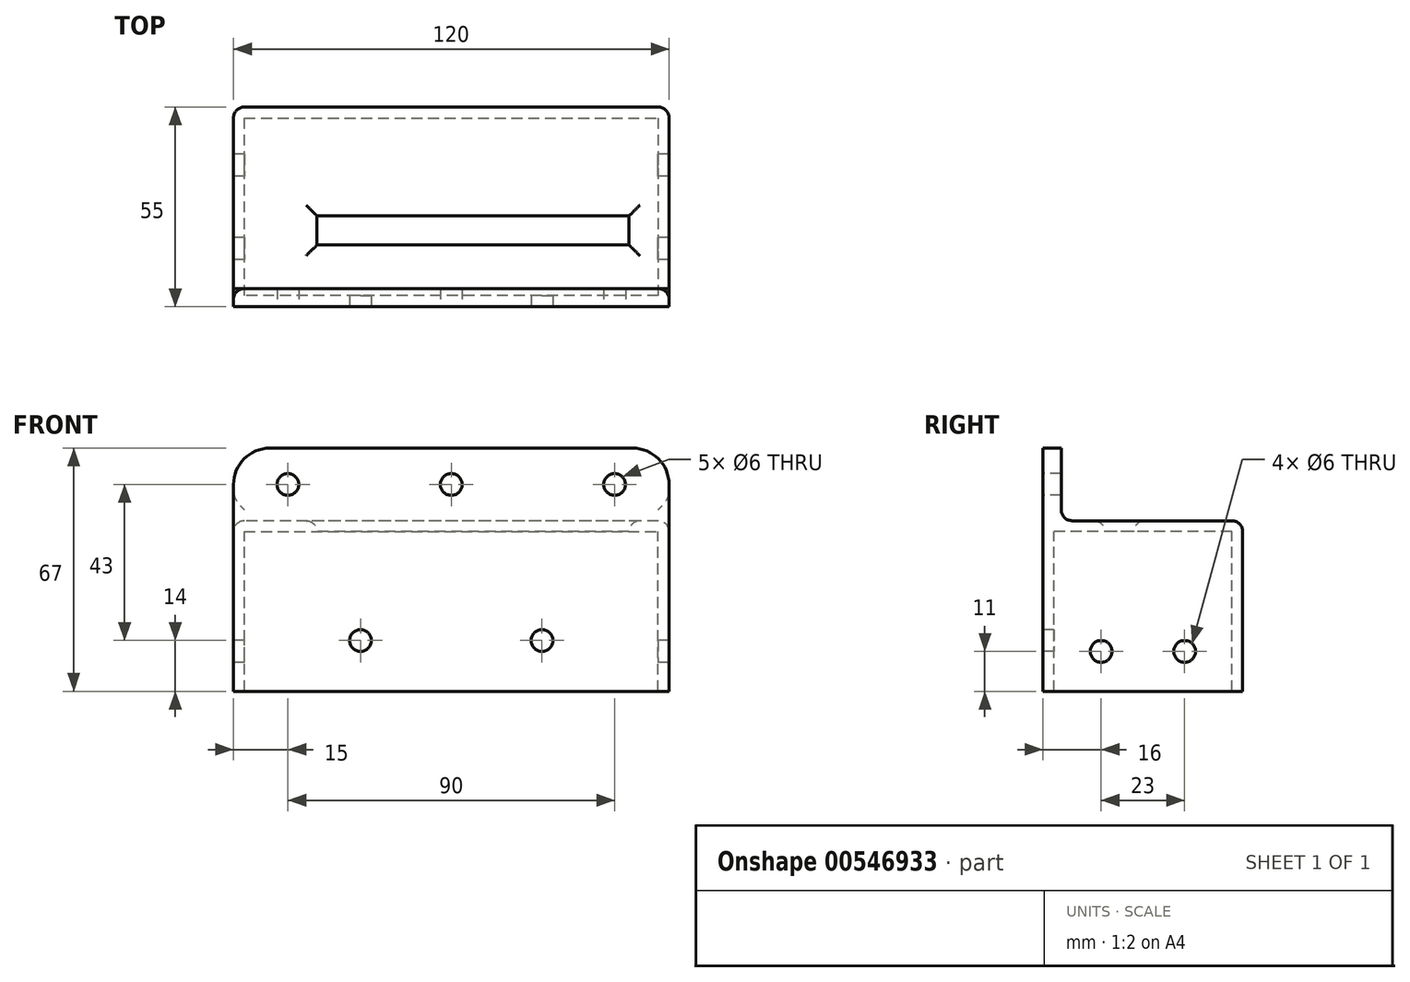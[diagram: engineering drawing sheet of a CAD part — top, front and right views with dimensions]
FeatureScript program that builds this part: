
annotation { "Feature Type Name" : "Feature", "Feature Type Description" : "" }
export const myFeature = defineFeature(function(context is Context, id is Id, definition is map)
    precondition{}
    {
        {
            var Q0;
            Q0=qCreatedBy(makeId("Top.planeOp"),FACE);
            var sketch = newSketch(context, id + "F0", { "sketchPlane" : qUnion([Q0])});
            skLineSegment(sketch, "E0", {"start": v(0, 0) * mm, "end": v(0, 55) * mm});
            skLineSegment(sketch, "E1", {"start": v(0, 55) * mm, "end": v(120, 55) * mm});
            skLineSegment(sketch, "E2", {"start": v(120, 55) * mm, "end": v(120, 0) * mm});
            skLineSegment(sketch, "E3", {"start": v(120, 0) * mm, "end": v(0, 0) * mm});
            skLineSegment(sketch, "E4.0", {"start": v(3, 3) * mm, "end": v(3, 52) * mm});
            skLineSegment(sketch, "E5.0", {"start": v(117, 52) * mm, "end": v(117, 3) * mm});
            skLineSegment(sketch, "E6.0", {"start": v(3, 52) * mm, "end": v(117, 52) * mm});
            skLineSegment(sketch, "E7.0", {"start": v(117, 3) * mm, "end": v(3, 3) * mm});
            skLineSegment(sketch, "E8.0", {"start": v(109, 17) * mm, "end": v(23, 17) * mm});
            skLineSegment(sketch, "E9.0", {"start": v(109, 25) * mm, "end": v(23, 25) * mm});
            skLineSegment(sketch, "E10.0", {"start": v(23, 17) * mm, "end": v(23, 25) * mm});
            skLineSegment(sketch, "E11.0", {"start": v(109, 25) * mm, "end": v(109, 17) * mm});
            skSolve(sketch);
        }
        {
            var Q0;
            Q0=makeQuery(id+"F0.imprint","IMPRINT",FACE,{"disambiguationData":[TD([[makeQuery(id+"F0.imprint","IMPRINT",EDGE,{"derivedFrom":sQuery(id+"F0.wireOp",EDGE,"E4.0")}),-1.0]])]});
            extrude(context, id + "F1", {"entities" : qUnion([Q0]), "oppositeDirection" : true, "depth" : 3 * mm, "offsetDistance" : 25 * mm});
        }
        {
            var Q0;
            Q0=makeQuery(id+"F0.imprint","IMPRINT",FACE,{"disambiguationData":[TD([[makeQuery(id+"F0.imprint","IMPRINT",EDGE,{"derivedFrom":sQuery(id+"F0.wireOp",EDGE,"E0")}),-1.0]])]});
            extrude(context, id + "F2", {"entities" : qUnion([Q0]), "operationType" : NewBodyOperationType.ADD, "oppositeDirection" : true, "depth" : 47 * mm, "offsetDistance" : 25 * mm});
        }
        {
            var Q0;
            Q0=qCreatedBy(makeId("Right.planeOp"),FACE);
            var sketch = newSketch(context, id + "F3", { "sketchPlane" : qUnion([Q0])});
            skLineSegment(sketch, "E12", {"start": v(0, 0) * mm, "end": v(0, -36) * mm, "construction": true});
            skLineSegment(sketch, "E13", {"start": v(0, -36) * mm, "end": v(55, -36) * mm, "construction": true});
            skLineSegment(sketch, "E14.0", {"start": v(27.5, 0) * mm, "end": v(27.5, -36) * mm, "construction": true});
            skLineSegment(sketch, "E15.0", {"start": v(16, 0) * mm, "end": v(16, -36) * mm, "construction": true});
            skLineSegment(sketch, "E16.0", {"start": v(39, 0) * mm, "end": v(39, -36) * mm, "construction": true});
            skCircle(sketch, "E17", {"center": v(39, -36) * mm, "radius": 3 * mm});
            skCircle(sketch, "E18", {"center": v(16, -36) * mm, "radius": 3 * mm});
            skSolve(sketch);
        }
        {
            var Q0;
            Q0=makeQuery(id+"F3.imprint","IMPRINT",FACE,{"disambiguationData":[TD([[makeQuery(id+"F3.imprint","IMPRINT",EDGE,{"derivedFrom":sQuery(id+"F3.wireOp",EDGE,"E17")}),1.0]])]});
            var Q1;
            Q1=makeQuery(id+"F3.imprint","IMPRINT",FACE,{"disambiguationData":[TD([[makeQuery(id+"F3.imprint","IMPRINT",EDGE,{"derivedFrom":sQuery(id+"F3.wireOp",EDGE,"E18")}),1.0]])]});
            extrude(context, id + "F4", {"entities" : qUnion([Q0, Q1]), "operationType" : NewBodyOperationType.REMOVE, "depth" : 130 * mm, "offsetDistance" : 25 * mm});
        }
        {
            var Q0;
            Q0=qCreatedBy(makeId("Front.planeOp"),FACE);
            var sketch = newSketch(context, id + "F5", { "sketchPlane" : qUnion([Q0])});
            skLineSegment(sketch, "E19", {"start": v(0, 0) * mm, "end": v(120, 0) * mm, "construction": true});
            skLineSegment(sketch, "E20", {"start": v(0, 0) * mm, "end": v(0, -33) * mm, "construction": true});
            skLineSegment(sketch, "E21", {"start": v(0, -33) * mm, "end": v(122.32, -33) * mm, "construction": true});
            skLineSegment(sketch, "E22.0", {"start": v(60, 0) * mm, "end": v(60, -33) * mm, "construction": true});
            skLineSegment(sketch, "E23.0", {"start": v(35, 0) * mm, "end": v(35, -33) * mm, "construction": true});
            skLineSegment(sketch, "E24.0", {"start": v(85, 0) * mm, "end": v(85, -33) * mm, "construction": true});
            skCircle(sketch, "E25", {"center": v(35, -33) * mm, "radius": 3 * mm});
            skCircle(sketch, "E26", {"center": v(85, -33) * mm, "radius": 3 * mm});
            skSolve(sketch);
        }
        {
            var Q0;
            Q0=makeQuery(id+"F5.imprint","IMPRINT",FACE,{"disambiguationData":[TD([[makeQuery(id+"F5.imprint","IMPRINT",EDGE,{"derivedFrom":sQuery(id+"F5.wireOp",EDGE,"E25")}),1.0]])]});
            var Q1;
            Q1=makeQuery(id+"F5.imprint","IMPRINT",FACE,{"disambiguationData":[TD([[makeQuery(id+"F5.imprint","IMPRINT",EDGE,{"derivedFrom":sQuery(id+"F5.wireOp",EDGE,"E26")}),1.0]])]});
            extrude(context, id + "F6", {"entities" : qUnion([Q0, Q1]), "operationType" : NewBodyOperationType.REMOVE, "oppositeDirection" : true, "depth" : 10 * mm, "offsetDistance" : 25 * mm});
        }
        {
            var Q0;
            Q0=qCreatedBy(makeId("Right.planeOp"),FACE);
            var sketch = newSketch(context, id + "F7", { "sketchPlane" : qUnion([Q0])});
            skLineSegment(sketch, "E27", {"start": v(0, 0) * mm, "end": v(0, 20) * mm});
            skLineSegment(sketch, "E28", {"start": v(0, 20) * mm, "end": v(5, 20) * mm});
            skLineSegment(sketch, "E29", {"start": v(5, 20) * mm, "end": v(5, 0) * mm});
            skLineSegment(sketch, "E30", {"start": v(5, 0) * mm, "end": v(0, 0) * mm});
            skSolve(sketch);
        }
        {
            var Q0;
            Q0=makeQuery(id+"F7.imprint","IMPRINT",FACE,{"disambiguationData":[TD([[makeQuery(id+"F7.imprint","IMPRINT",EDGE,{"derivedFrom":sQuery(id+"F7.wireOp",EDGE,"E27")}),-1.0]])]});
            extrude(context, id + "F8", {"entities" : qUnion([Q0]), "operationType" : NewBodyOperationType.ADD, "depth" : 120 * mm, "offsetDistance" : 25 * mm});
        }
        {
            var Q0;
            Q0=qCreatedBy(makeId("Front.planeOp"),FACE);
            var sketch = newSketch(context, id + "F9", { "sketchPlane" : qUnion([Q0])});
            skLineSegment(sketch, "E31", {"start": v(0, 0) * mm, "end": v(0, 10) * mm, "construction": true});
            skLineSegment(sketch, "E32", {"start": v(0, 10) * mm, "end": v(120, 10) * mm, "construction": true});
            skLineSegment(sketch, "E33", {"start": v(120, 10) * mm, "end": v(120, 0) * mm, "construction": true});
            skLineSegment(sketch, "E34.0", {"start": v(15, 0) * mm, "end": v(15, 10) * mm, "construction": true});
            skLineSegment(sketch, "E35.0", {"start": v(105, 10) * mm, "end": v(105, 0) * mm, "construction": true});
            skLineSegment(sketch, "E36.0", {"start": v(60, 10) * mm, "end": v(60, 0) * mm, "construction": true});
            skCircle(sketch, "E37", {"center": v(15, 10) * mm, "radius": 3 * mm});
            skCircle(sketch, "E38", {"center": v(60, 10) * mm, "radius": 3 * mm});
            skCircle(sketch, "E39", {"center": v(105, 10) * mm, "radius": 3 * mm});
            skSolve(sketch);
        }
        {
            var Q0;
            Q0=makeQuery(id+"F9.imprint","IMPRINT",FACE,{"disambiguationData":[TD([[makeQuery(id+"F9.imprint","IMPRINT",EDGE,{"derivedFrom":sQuery(id+"F9.wireOp",EDGE,"E37")}),1.0]])]});
            var Q1;
            Q1=makeQuery(id+"F9.imprint","IMPRINT",FACE,{"disambiguationData":[TD([[makeQuery(id+"F9.imprint","IMPRINT",EDGE,{"derivedFrom":sQuery(id+"F9.wireOp",EDGE,"E38")}),1.0]])]});
            var Q2;
            Q2=makeQuery(id+"F9.imprint","IMPRINT",FACE,{"disambiguationData":[TD([[makeQuery(id+"F9.imprint","IMPRINT",EDGE,{"derivedFrom":sQuery(id+"F9.wireOp",EDGE,"E39")}),1.0]])]});
            extrude(context, id + "F10", {"entities" : qUnion([Q0, Q1, Q2]), "operationType" : NewBodyOperationType.REMOVE, "oppositeDirection" : true, "depth" : 25 * mm, "offsetDistance" : 25 * mm});
        }
        {
            var Q0;
            Q0=makeQuery(id+"F8.opExtrude","CAP_EDGE",EDGE,{"disambiguationData":[OSD([sQuery(id+"F7.wireOp",EDGE,"E28")])],"isStart":true});
            var Q1;
            Q1=makeQuery(id+"F8.opExtrude","CAP_EDGE",EDGE,{"disambiguationData":[OSD([sQuery(id+"F7.wireOp",EDGE,"E28")])],"isStart":false});
            fillet(context, id + "F11", {"entities" : qUnion([Q0, Q1]), "radius" : 10 * mm, "tangentPropagation" : true, "allowEdgeOverflow" : false});
        }
        {
            var Q0;
            Q0=makeQuery(id+"F1.opExtrude","CAP_EDGE",EDGE,{"disambiguationData":[OSD([sQuery(id+"F0.wireOp",EDGE,"E8.0")])],"isStart":true});
            var Q1;
            {var subQ0=sQuery(id+"F0.wireOp",EDGE,"E7.0");var subQ1=sQuery(id+"F0.wireOp",EDGE,"E6.0");var subQ2=sQuery(id+"F0.wireOp",EDGE,"E5.0");var subQ3=sQuery(id+"F0.wireOp",EDGE,"E4.0");Q1=makeQuery(id+"F2.boolean.opBoolean","MERGE",FACE,{"derivedFrom":[makeQuery(id+"F1.opExtrude","CAP_FACE",FACE,{"disambiguationData":[OSD([subQ3,subQ2,subQ1,subQ0,sQuery(id+"F0.wireOp",EDGE,"E8.0"),sQuery(id+"F0.wireOp",EDGE,"E9.0"),sQuery(id+"F0.wireOp",EDGE,"E10.0"),sQuery(id+"F0.wireOp",EDGE,"E11.0")])],"isStart":true}),makeQuery(id+"F2.opExtrude","CAP_FACE",FACE,{"disambiguationData":[OSD([sQuery(id+"F0.wireOp",EDGE,"E0"),sQuery(id+"F0.wireOp",EDGE,"E1"),sQuery(id+"F0.wireOp",EDGE,"E2"),sQuery(id+"F0.wireOp",EDGE,"E3"),subQ3,subQ2,subQ1,subQ0])],"isStart":true})]});}
            var Q2;
            Q2=makeQuery(id+"F2.opExtrude","SWEPT_EDGE",EDGE,{"disambiguationData":[OSD([sQuery(id+"F0.wireOp",EDGE,"E1"),sQuery(id+"F0.wireOp",EDGE,"E2")])]});
            var Q3;
            Q3=makeQuery(id+"F2.opExtrude","SWEPT_EDGE",EDGE,{"disambiguationData":[OSD([sQuery(id+"F0.wireOp",EDGE,"E0"),sQuery(id+"F0.wireOp",EDGE,"E1")])]});
            fillet(context, id + "F12", {"entities" : qUnion([Q0, Q1, Q2, Q3]), "radius" : 3 * mm, "tangentPropagation" : true, "allowEdgeOverflow" : false});
        }
    });
